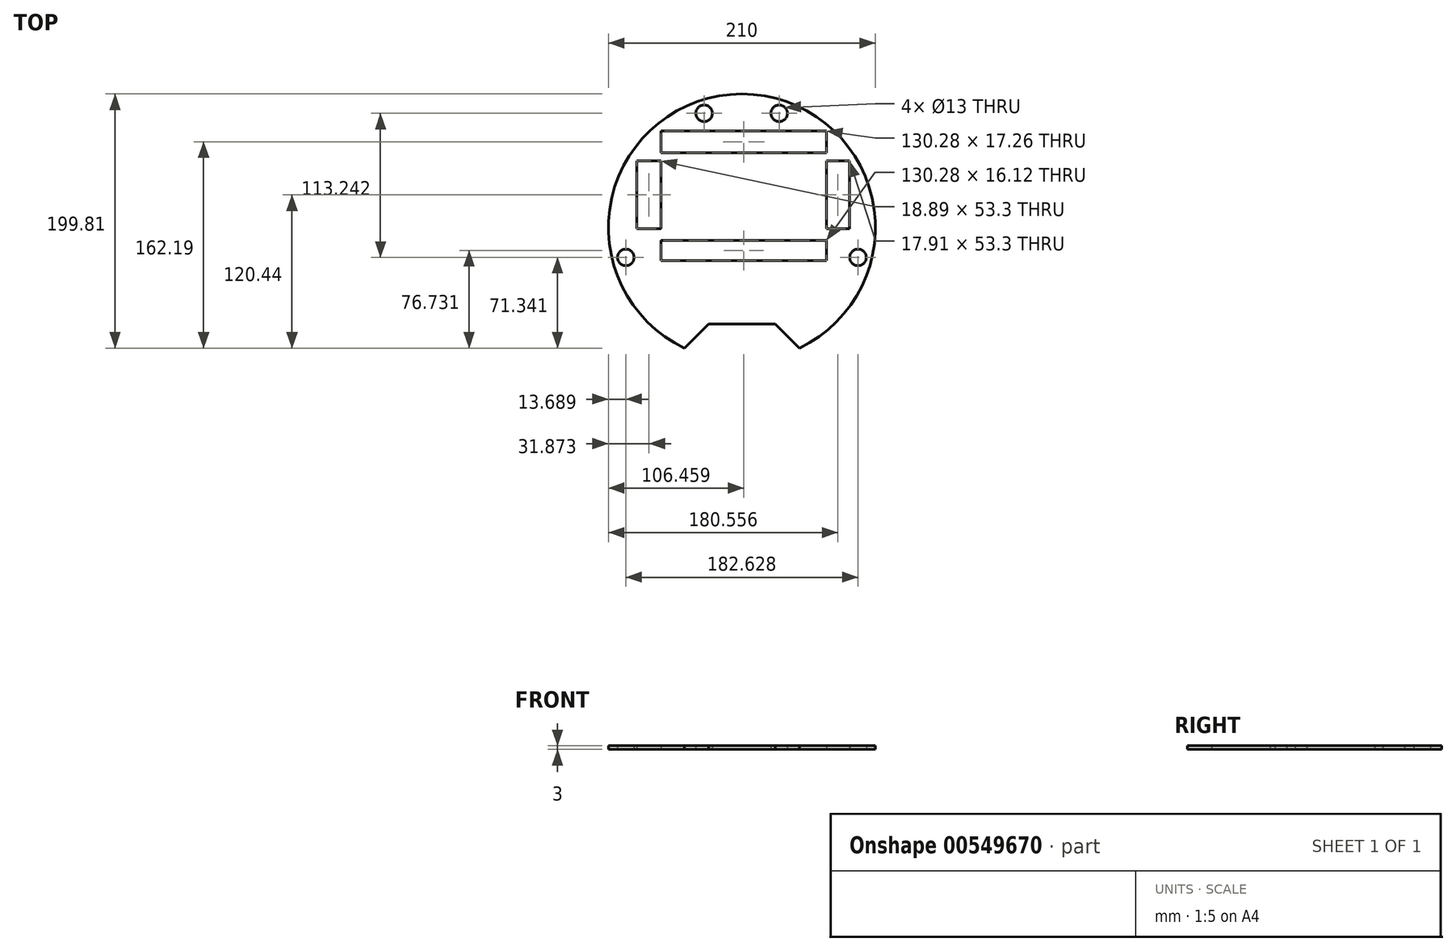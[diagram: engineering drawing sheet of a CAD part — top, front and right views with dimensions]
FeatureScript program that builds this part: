
annotation { "Feature Type Name" : "Feature", "Feature Type Description" : "" }
export const myFeature = defineFeature(function(context is Context, id is Id, definition is map)
    precondition{}
    {
        {
            var Q0;
            Q0=qCreatedBy(makeId("Top.planeOp"),FACE);
            var sketch = newSketch(context, id + "F0", { "sketchPlane" : qUnion([Q0])});
            skCircle(sketch, "E0", {"center": v(-0.03, 1.02) * mm, "radius": 105 * mm});
            skLineSegment(sketch, "E1", {"start": v(-0.03, 106.02) * mm, "end": v(-0.03, -103.98) * mm});
            skLineSegment(sketch, "E2", {"start": v(-0.03, 1.02) * mm, "end": v(-0.03, 106.02) * mm});
            skCircle(sketch, "E3", {"center": v(-29.75, 90.8) * mm, "radius": 6.5 * mm});
            skCircle(sketch, "E4", {"center": v(29.27, 90.8) * mm, "radius": 6.5 * mm});
            skCircle(sketch, "E5", {"center": v(-91.34, -22.45) * mm, "radius": 6.5 * mm});
            skCircle(sketch, "E6", {"center": v(91.29, -22.45) * mm, "radius": 6.5 * mm});
            skLineSegment(sketch, "E7", {"start": v(-0.03, -48.65) * mm, "end": v(-0.03, -63.7) * mm});
            skLineSegment(sketch, "E8", {"start": v(-26.15, -74.78) * mm, "end": v(26.1, -74.78) * mm});
            skLineSegment(sketch, "E9", {"start": v(-26.15, -74.78) * mm, "end": v(-45.16, -93.79) * mm});
            skLineSegment(sketch, "E10", {"start": v(26.1, -74.78) * mm, "end": v(45.1, -93.79) * mm});
            skLineSegment(sketch, "E11.bottom", {"start": v(-50.83, 53.3) * mm, "end": v(50.77, 53.3) * mm});
            skLineSegment(sketch, "E11.top", {"start": v(-50.83, 0) * mm, "end": v(50.77, 0) * mm});
            skLineSegment(sketch, "E11.left", {"start": v(-50.83, 53.3) * mm, "end": v(-50.83, 0) * mm});
            skLineSegment(sketch, "E11.right", {"start": v(50.77, 53.3) * mm, "end": v(50.77, 0) * mm});
            skLineSegment(sketch, "E12.bottom", {"start": v(-63.71, 77.03) * mm, "end": v(66.57, 77.03) * mm});
            skLineSegment(sketch, "E12.top", {"start": v(-63.71, 59.77) * mm, "end": v(66.57, 59.77) * mm});
            skLineSegment(sketch, "E12.left", {"start": v(-63.71, 77.03) * mm, "end": v(-63.71, 59.77) * mm});
            skLineSegment(sketch, "E12.right", {"start": v(66.57, 77.03) * mm, "end": v(66.57, 59.77) * mm});
            skPoint(sketch, "E13.firstSnap0", {"position": v(-0.03, 53.3) * mm});
            skLineSegment(sketch, "E13.bottom", {"start": v(66.57, 53.3) * mm, "end": v(84.48, 53.3) * mm});
            skLineSegment(sketch, "E13.top", {"start": v(66.57, 0) * mm, "end": v(84.48, 0) * mm});
            skLineSegment(sketch, "E13.left", {"start": v(66.57, 53.3) * mm, "end": v(66.57, 0) * mm});
            skLineSegment(sketch, "E13.right", {"start": v(84.48, 53.3) * mm, "end": v(84.48, 0) * mm});
            skLineSegment(sketch, "E14.bottom", {"start": v(-63.71, 53.3) * mm, "end": v(-82.6, 53.3) * mm});
            skLineSegment(sketch, "E14.top", {"start": v(-63.71, 0) * mm, "end": v(-82.6, 0) * mm});
            skLineSegment(sketch, "E14.left", {"start": v(-63.71, 53.3) * mm, "end": v(-63.71, 0) * mm});
            skLineSegment(sketch, "E14.right", {"start": v(-82.6, 53.3) * mm, "end": v(-82.6, 0) * mm});
            skLineSegment(sketch, "E15.bottom", {"start": v(-63.71, -9) * mm, "end": v(66.57, -9) * mm});
            skLineSegment(sketch, "E15.top", {"start": v(-63.71, -25.12) * mm, "end": v(66.57, -25.12) * mm});
            skLineSegment(sketch, "E15.left", {"start": v(-63.71, -9) * mm, "end": v(-63.71, -25.12) * mm});
            skLineSegment(sketch, "E15.right", {"start": v(66.57, -9) * mm, "end": v(66.57, -25.12) * mm});
            skSolve(sketch);
        }
        {
            var Q0;
            Q0=makeQuery(id+"F0.imprint","IMPRINT",FACE,{"disambiguationData":[TD([[makeQuery(id+"F0.imprint","IMPRINT",EDGE,{"derivedFrom":sQuery(id+"F0.wireOp",EDGE,"E3")}),-1.0]])]});
            var Q1;
            Q1=makeQuery(id+"F0.imprint","IMPRINT",FACE,{"disambiguationData":[TD([[makeQuery(id+"F0.imprint","IMPRINT",EDGE,{"derivedFrom":sQuery(id+"F0.wireOp",EDGE,"E4")}),-1.0]])]});
            var Q2;
            {var subQ0=sQuery(id+"F0.wireOp",EDGE,"E11.right");Q2=makeQuery(id+"F0.imprint","IMPRINT",FACE,{"disambiguationData":[TD([[makeQuery(id+"F0.imprint","IMPRINT",EDGE,{"derivedFrom":subQ0}),-1.0]])]});}
            var Q3;
            {var subQ0=sQuery(id+"F0.wireOp",EDGE,"E11.left");Q3=makeQuery(id+"F0.imprint","IMPRINT",FACE,{"disambiguationData":[TD([[makeQuery(id+"F0.imprint","IMPRINT",EDGE,{"derivedFrom":subQ0}),1.0]])]});}
            extrude(context, id + "F1", {"entities" : qUnion([Q0, Q1, Q2, Q3]), "depth" : 3 * mm, "offsetDistance" : 25.4 * mm});
        }
    });
